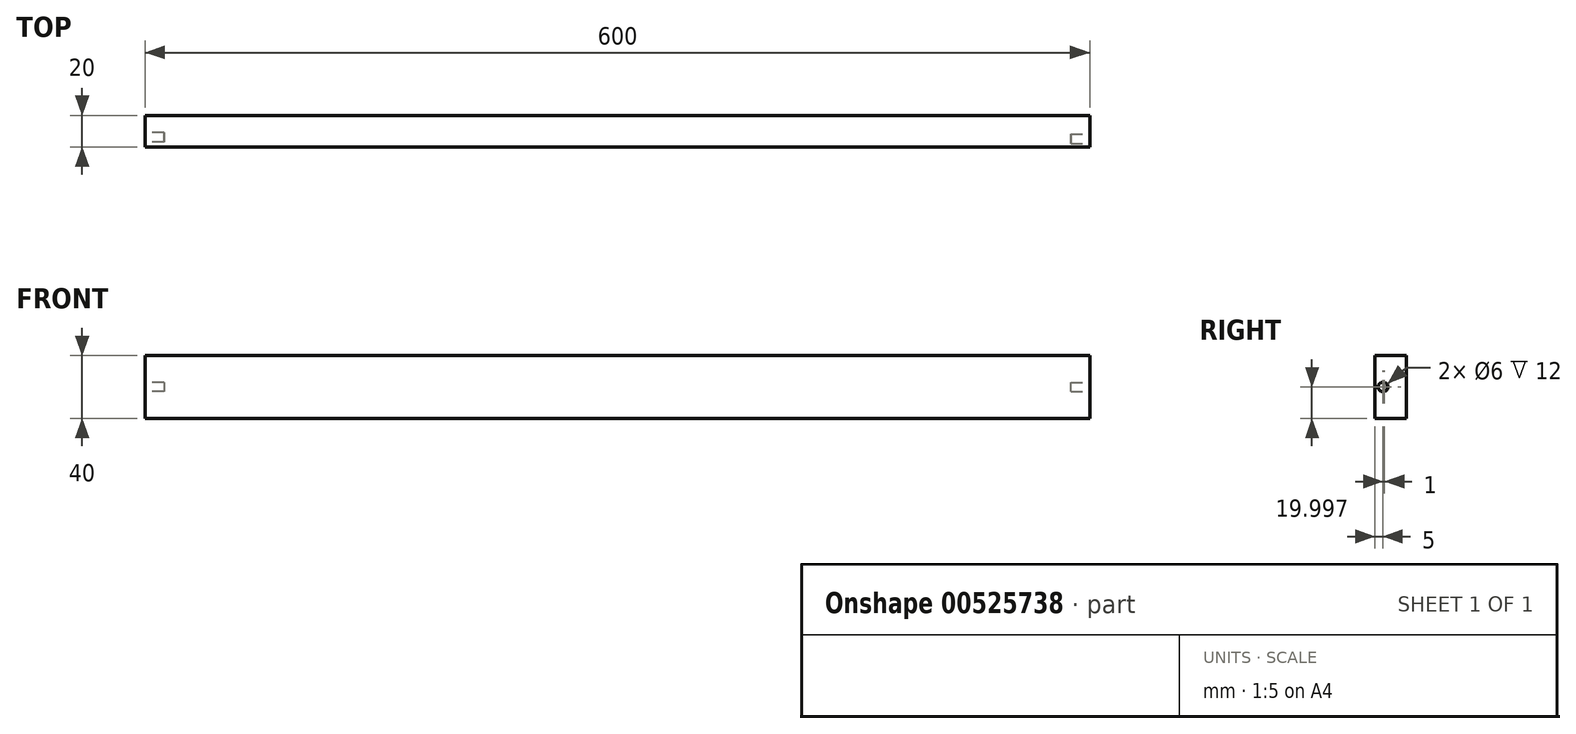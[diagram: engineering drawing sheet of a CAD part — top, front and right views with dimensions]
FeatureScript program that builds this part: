
annotation { "Feature Type Name" : "Feature", "Feature Type Description" : "" }
export const myFeature = defineFeature(function(context is Context, id is Id, definition is map)
    precondition{}
    {
        {
            var Q0;
            Q0=qCreatedBy(makeId("Front.planeOp"),FACE);
            var sketch = newSketch(context, id + "F0", { "sketchPlane" : qUnion([Q0])});
            skLineSegment(sketch, "E0.bottom", {"start": v(-123.29, 79.18) * mm, "end": v(476.71, 79.18) * mm});
            skLineSegment(sketch, "E0.top", {"start": v(-123.29, 39.18) * mm, "end": v(476.71, 39.18) * mm});
            skLineSegment(sketch, "E0.left", {"start": v(-123.29, 79.18) * mm, "end": v(-123.29, 39.18) * mm});
            skLineSegment(sketch, "E0.right", {"start": v(476.71, 79.18) * mm, "end": v(476.71, 39.18) * mm});
            skSolve(sketch);
        }
        {
            var Q0;
            Q0 = qSketchRegion(id + "F0", true);
            extrude(context, id + "F1", {"entities" : qUnion([Q0]), "depth" : 20 * mm, "offsetDistance" : 25 * mm});
        }
        {
            var Q0;
            Q0=makeQuery(id+"F1.opExtrude","SWEPT_FACE",FACE,{"disambiguationData":[OSD([sQuery(id+"F0.wireOp",EDGE,"E0.right")])]});
            var sketch = newSketch(context, id + "F2", { "sketchPlane" : qUnion([Q0])});
            skCircle(sketch, "E1", {"center": v(-15, 59.18) * mm, "radius": 3 * mm});
            skSolve(sketch);
        }
        {
            var Q0;
            Q0=makeQuery(id+"F2.imprint","IMPRINT",FACE,{"disambiguationData":[TD([[makeQuery(id+"F2.imprint","IMPRINT",EDGE,{"derivedFrom":sQuery(id+"F2.wireOp",EDGE,"E1")}),1.0]])]});
            extrude(context, id + "F3", {"entities" : qUnion([Q0]), "operationType" : NewBodyOperationType.REMOVE, "oppositeDirection" : true, "depth" : 12 * mm, "offsetDistance" : 25 * mm});
        }
        {
            var Q0;
            Q0=makeQuery(id+"F1.opExtrude","SWEPT_FACE",FACE,{"disambiguationData":[OSD([sQuery(id+"F0.wireOp",EDGE,"E0.left")])]});
            var sketch = newSketch(context, id + "F4", { "sketchPlane" : qUnion([Q0])});
            skCircle(sketch, "E2", {"center": v(14, 59.18) * mm, "radius": 3 * mm});
            skPoint(sketch, "E2.centerSnap0", {"position": v(20, 59.18) * mm});
            skSolve(sketch);
        }
        {
            var Q0;
            Q0 = qSketchRegion(id + "F4", true);
            extrude(context, id + "F5", {"entities" : qUnion([Q0]), "operationType" : NewBodyOperationType.REMOVE, "oppositeDirection" : true, "depth" : 12 * mm, "offsetDistance" : 25 * mm});
        }
    });
